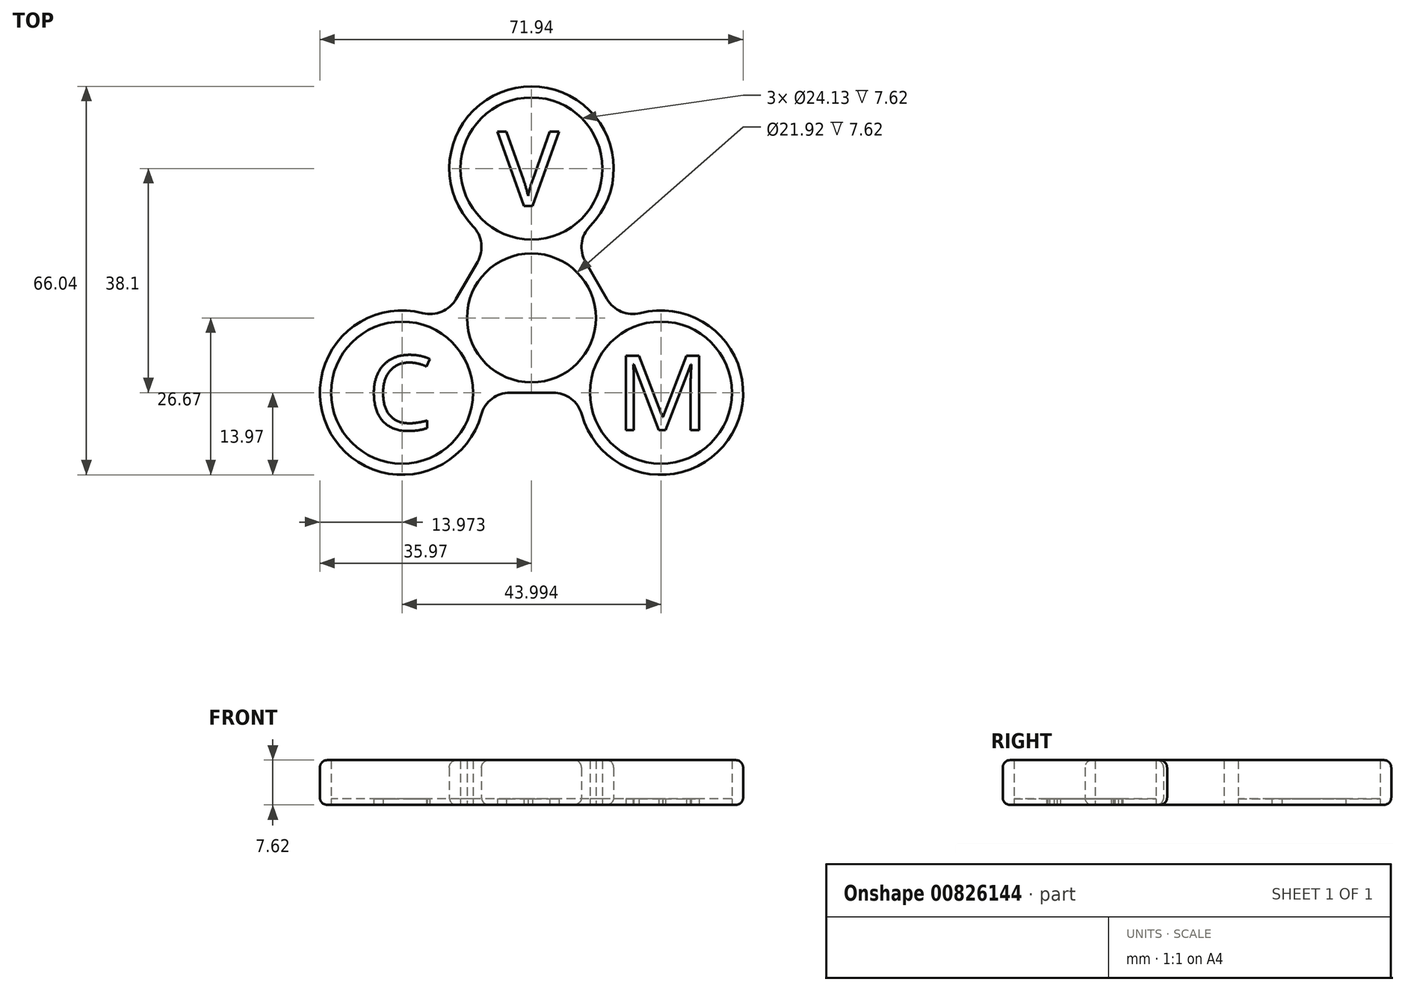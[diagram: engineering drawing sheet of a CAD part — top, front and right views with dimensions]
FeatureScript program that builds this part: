
annotation { "Feature Type Name" : "Feature", "Feature Type Description" : "" }
export const myFeature = defineFeature(function(context is Context, id is Id, definition is map)
    precondition{}
    {
        {
            var Q0;
            Q0=qCreatedBy(makeId("Top.planeOp"),FACE);
            var sketch = newSketch(context, id + "F0", { "sketchPlane" : qUnion([Q0])});
            skCircle(sketch, "E0.cCircle", {"center": v(0, 0) * mm, "radius": 12.7 * mm, "construction": true});
            skLineSegment(sketch, "E0.0", {"start": v(22, -12.7) * mm, "end": v(-22, -12.7) * mm});
            skLineSegment(sketch, "E0.1", {"start": v(-22, -12.7) * mm, "end": v(0, 25.4) * mm});
            skLineSegment(sketch, "E0.2", {"start": v(0, 25.4) * mm, "end": v(22, -12.7) * mm});
            skPoint(sketch, "E0.0.midPoint", {"position": v(0, -12.7) * mm});
            skCircle(sketch, "E1", {"center": v(0, 25.4) * mm, "radius": 13.97 * mm});
            skCircle(sketch, "E2", {"center": v(-22, -12.7) * mm, "radius": 13.97 * mm});
            skCircle(sketch, "E3", {"center": v(22, -12.7) * mm, "radius": 13.97 * mm});
            skCircle(sketch, "E4", {"center": v(0, 0) * mm, "radius": 10.96 * mm});
            skCircle(sketch, "E5", {"center": v(0, 25.4) * mm, "radius": 12.07 * mm});
            skCircle(sketch, "E6", {"center": v(-22, -12.7) * mm, "radius": 12.07 * mm});
            skCircle(sketch, "E7", {"center": v(22, -12.7) * mm, "radius": 12.07 * mm});
            skText(sketch, "E8", { "text": "C", "fontName": "OpenSans-Regular.ttf"});
            skText(sketch, "E9", { "text": "M", "fontName": "OpenSans-Regular.ttf"});
            skText(sketch, "E10", { "text": "V", "fontName": "OpenSans-Regular.ttf"});
            const initialGuessF0  = {"E8": [-0.02787, -0.01905, 1, 0, 0.0127], "E9": [0.01432, -0.01905, 1, 0, 0.0127], "E10": [-0.00582, 0.01905, 1, 0, 0.0127]};
            skSetInitialGuess(sketch, initialGuessF0);
            skSolve(sketch);
        }
        {
            var Q0;
            {var subQ0=sQuery(id+"F0.wireOp",EDGE,"E0.1");var subQ1=sQuery(id+"F0.wireOp",EDGE,"E0.0");var subQ2=makeQuery(id+"F0.imprint","INTERSECT",VERTEX,{"derivedFrom":[subQ1,subQ0]});Q0=makeQuery(id+"F0.imprint","IMPRINT",FACE,{"disambiguationData":[TD([[makeQuery(id+"F0.imprint","IMPRINT",EDGE,{"disambiguationData":[TD([[subQ2,1.0]])],"derivedFrom":subQ1}),1.0]])]});}
            var Q1;
            {var subQ0=sQuery(id+"F0.wireOp",EDGE,"E0.2");var subQ1=sQuery(id+"F0.wireOp",EDGE,"E0.0");var subQ2=makeQuery(id+"F0.imprint","INTERSECT",VERTEX,{"derivedFrom":[subQ1,subQ0]});Q1=makeQuery(id+"F0.imprint","IMPRINT",FACE,{"disambiguationData":[TD([[makeQuery(id+"F0.imprint","IMPRINT",EDGE,{"disambiguationData":[TD([[subQ2,-1.0]])],"derivedFrom":subQ1}),-1.0]])]});}
            var Q2;
            {var subQ0=sQuery(id+"F0.wireOp",EDGE,"E0.2");var subQ1=sQuery(id+"F0.wireOp",EDGE,"E0.0");var subQ2=makeQuery(id+"F0.imprint","INTERSECT",VERTEX,{"derivedFrom":[subQ1,subQ0]});Q2=makeQuery(id+"F0.imprint","IMPRINT",FACE,{"disambiguationData":[TD([[makeQuery(id+"F0.imprint","IMPRINT",EDGE,{"disambiguationData":[TD([[subQ2,-1.0]])],"derivedFrom":subQ1}),1.0]])]});}
            var Q3;
            {var subQ0=sQuery(id+"F0.wireOp",EDGE,"E0.2");var subQ1=sQuery(id+"F0.wireOp",EDGE,"E0.1");var subQ2=makeQuery(id+"F0.imprint","INTERSECT",VERTEX,{"derivedFrom":[subQ1,subQ0]});Q3=makeQuery(id+"F0.imprint","IMPRINT",FACE,{"disambiguationData":[TD([[makeQuery(id+"F0.imprint","IMPRINT",EDGE,{"disambiguationData":[TD([[subQ2,1.0]])],"derivedFrom":subQ1}),-1.0]])]});}
            var Q4;
            {var subQ0=sQuery(id+"F0.wireOp",EDGE,"E0.2");var subQ1=sQuery(id+"F0.wireOp",EDGE,"E0.1");var subQ2=makeQuery(id+"F0.imprint","INTERSECT",VERTEX,{"derivedFrom":[subQ1,subQ0]});Q4=makeQuery(id+"F0.imprint","IMPRINT",FACE,{"disambiguationData":[TD([[makeQuery(id+"F0.imprint","IMPRINT",EDGE,{"disambiguationData":[TD([[subQ2,1.0]])],"derivedFrom":subQ1}),1.0]])]});}
            var Q5;
            {var subQ0=sQuery(id+"F0.wireOp",EDGE,"E0.1");var subQ1=sQuery(id+"F0.wireOp",EDGE,"E0.0");var subQ2=makeQuery(id+"F0.imprint","INTERSECT",VERTEX,{"derivedFrom":[subQ1,subQ0]});Q5=makeQuery(id+"F0.imprint","IMPRINT",FACE,{"disambiguationData":[TD([[makeQuery(id+"F0.imprint","IMPRINT",EDGE,{"disambiguationData":[TD([[subQ2,1.0]])],"derivedFrom":subQ1}),-1.0]])]});}
            var Q6;
            {var subQ0=sQuery(id+"F0.wireOp",EDGE,"E10.sketch_text.stroke-2");Q6=makeQuery(id+"F0.imprint","IMPRINT",FACE,{"disambiguationData":[TD([[makeQuery(id+"F0.imprint","IMPRINT",EDGE,{"derivedFrom":subQ0}),1.0]])]});}
            var Q7;
            {var subQ1=sQuery(id+"F0.wireOp",EDGE,"E9.sketch_text.stroke-1");Q7=makeQuery(id+"F0.imprint","IMPRINT",FACE,{"disambiguationData":[TD([[makeQuery(id+"F0.imprint","IMPRINT",EDGE,{"derivedFrom":subQ1}),1.0]])]});}
            extrude(context, id + "F1", {"entities" : qUnion([Q0, Q1, Q2, Q3, Q4, Q5, Q6, Q7]), "depth" : 1.02 * mm, "offsetDistance" : 25.4 * mm});
        }
        {
            var Q0;
            {var subQ0=sQuery(id+"F0.wireOp",EDGE,"E1");var subQ1=sQuery(id+"F0.wireOp",EDGE,"E0.1");var subQ2=makeQuery(id+"F0.imprint","INTERSECT",VERTEX,{"derivedFrom":[subQ1,subQ0]});Q0=makeQuery(id+"F0.imprint","IMPRINT",FACE,{"disambiguationData":[TD([[makeQuery(id+"F0.imprint","IMPRINT",EDGE,{"disambiguationData":[TD([[subQ2,-1.0]])],"derivedFrom":subQ1}),1.0]])]});}
            var Q1;
            {var subQ0=sQuery(id+"F0.wireOp",EDGE,"E2");var subQ1=sQuery(id+"F0.wireOp",EDGE,"E0.0");var subQ2=makeQuery(id+"F0.imprint","INTERSECT",VERTEX,{"derivedFrom":[subQ1,subQ0]});Q1=makeQuery(id+"F0.imprint","IMPRINT",FACE,{"disambiguationData":[TD([[makeQuery(id+"F0.imprint","IMPRINT",EDGE,{"disambiguationData":[TD([[subQ2,-1.0]])],"derivedFrom":subQ1}),1.0]])]});}
            var Q2;
            {var subQ0=sQuery(id+"F0.wireOp",EDGE,"E3");var subQ1=sQuery(id+"F0.wireOp",EDGE,"E0.0");var subQ2=makeQuery(id+"F0.imprint","INTERSECT",VERTEX,{"derivedFrom":[subQ1,subQ0]});Q2=makeQuery(id+"F0.imprint","IMPRINT",FACE,{"disambiguationData":[TD([[makeQuery(id+"F0.imprint","IMPRINT",EDGE,{"disambiguationData":[TD([[subQ2,1.0]])],"derivedFrom":subQ1}),-1.0]])]});}
            var Q3;
            {var subQ0=sQuery(id+"F0.wireOp",EDGE,"E3");var subQ1=sQuery(id+"F0.wireOp",EDGE,"E0.0");var subQ2=makeQuery(id+"F0.imprint","INTERSECT",VERTEX,{"derivedFrom":[subQ1,subQ0]});Q3=makeQuery(id+"F0.imprint","IMPRINT",FACE,{"disambiguationData":[TD([[makeQuery(id+"F0.imprint","IMPRINT",EDGE,{"disambiguationData":[TD([[subQ2,1.0]])],"derivedFrom":subQ1}),1.0]])]});}
            var Q4;
            {var subQ0=sQuery(id+"F0.wireOp",EDGE,"E2");var subQ1=sQuery(id+"F0.wireOp",EDGE,"E0.0");var subQ2=makeQuery(id+"F0.imprint","INTERSECT",VERTEX,{"derivedFrom":[subQ1,subQ0]});Q4=makeQuery(id+"F0.imprint","IMPRINT",FACE,{"disambiguationData":[TD([[makeQuery(id+"F0.imprint","IMPRINT",EDGE,{"disambiguationData":[TD([[subQ2,-1.0]])],"derivedFrom":subQ1}),-1.0]])]});}
            var Q5;
            Q5=makeQuery(id+"F0.imprint","IMPRINT",FACE,{"disambiguationData":[TD([[makeQuery(id+"F0.imprint","IMPRINT",EDGE,{"derivedFrom":sQuery(id+"F0.wireOp",EDGE,"E4")}),-1.0]])]});
            var Q6;
            {var subQ0=sQuery(id+"F0.wireOp",EDGE,"E1");var subQ1=sQuery(id+"F0.wireOp",EDGE,"E0.1");var subQ2=makeQuery(id+"F0.imprint","INTERSECT",VERTEX,{"derivedFrom":[subQ1,subQ0]});Q6=makeQuery(id+"F0.imprint","IMPRINT",FACE,{"disambiguationData":[TD([[makeQuery(id+"F0.imprint","IMPRINT",EDGE,{"disambiguationData":[TD([[subQ2,-1.0]])],"derivedFrom":subQ1}),-1.0]])]});}
            extrude(context, id + "F2", {"entities" : qUnion([Q0, Q1, Q2, Q3, Q4, Q5, Q6]), "depth" : 7.62 * mm, "offsetDistance" : 25.4 * mm});
        }
        {
            var Q0;
            Q0=makeQuery(id+"F2.opExtrude","SWEPT_EDGE",EDGE,{"disambiguationData":[OSD([sQuery(id+"F0.wireOp",EDGE,"E0.1"),sQuery(id+"F0.wireOp",EDGE,"E2")])]});
            var Q1;
            Q1=makeQuery(id+"F2.opExtrude","SWEPT_EDGE",EDGE,{"disambiguationData":[OSD([sQuery(id+"F0.wireOp",EDGE,"E0.2"),sQuery(id+"F0.wireOp",EDGE,"E3")])]});
            var Q2;
            Q2=makeQuery(id+"F2.opExtrude","SWEPT_EDGE",EDGE,{"disambiguationData":[OSD([sQuery(id+"F0.wireOp",EDGE,"E0.2"),sQuery(id+"F0.wireOp",EDGE,"E1")])]});
            var Q3;
            Q3=makeQuery(id+"F2.opExtrude","SWEPT_EDGE",EDGE,{"disambiguationData":[OSD([sQuery(id+"F0.wireOp",EDGE,"E0.1"),sQuery(id+"F0.wireOp",EDGE,"E1")])]});
            var Q4;
            Q4=makeQuery(id+"F2.opExtrude","SWEPT_EDGE",EDGE,{"disambiguationData":[OSD([sQuery(id+"F0.wireOp",EDGE,"E0.0"),sQuery(id+"F0.wireOp",EDGE,"E3")])]});
            var Q5;
            Q5=makeQuery(id+"F2.opExtrude","SWEPT_EDGE",EDGE,{"disambiguationData":[OSD([sQuery(id+"F0.wireOp",EDGE,"E0.0"),sQuery(id+"F0.wireOp",EDGE,"E2")])]});
            fillet(context, id + "F3", {"entities" : qUnion([Q0, Q1, Q2, Q3, Q4, Q5]), "radius" : 5.08 * mm, "tangentPropagation" : true, "allowEdgeOverflow" : false});
        }
        {
            var Q0;
            Q0=makeQuery(id+"F2.opExtrude","CAP_EDGE",EDGE,{"disambiguationData":[OSD([sQuery(id+"F0.wireOp",EDGE,"E1")])],"isStart":false});
            var Q1;
            {var subQ0=sQuery(id+"F0.wireOp",EDGE,"E1");var subQ1=sQuery(id+"F0.wireOp",EDGE,"E0.1");Q1=makeQuery(id+"F3.opFillet","BLEND_EDGE",EDGE,{"blendedFrom":[makeQuery(id+"F2.opExtrude","SWEPT_EDGE",EDGE,{"disambiguationData":[OSD([subQ1,subQ0])]}),makeQuery(id+"F2.opExtrude","CAP_FACE",FACE,{"disambiguationData":[OSD([sQuery(id+"F0.wireOp",EDGE,"E0.0"),subQ1,sQuery(id+"F0.wireOp",EDGE,"E0.2"),subQ0,sQuery(id+"F0.wireOp",EDGE,"E2"),sQuery(id+"F0.wireOp",EDGE,"E3"),sQuery(id+"F0.wireOp",EDGE,"E4"),sQuery(id+"F0.wireOp",EDGE,"E5"),sQuery(id+"F0.wireOp",EDGE,"E6"),sQuery(id+"F0.wireOp",EDGE,"E7")])],"isStart":true})],"blendedInto":[makeQuery(id+"F2.opExtrude","CAP_FACE",FACE,{"disambiguationData":[OSD([sQuery(id+"F0.wireOp",EDGE,"E0.0"),subQ1,sQuery(id+"F0.wireOp",EDGE,"E0.2"),subQ0,sQuery(id+"F0.wireOp",EDGE,"E2"),sQuery(id+"F0.wireOp",EDGE,"E3"),sQuery(id+"F0.wireOp",EDGE,"E4"),sQuery(id+"F0.wireOp",EDGE,"E5"),sQuery(id+"F0.wireOp",EDGE,"E6"),sQuery(id+"F0.wireOp",EDGE,"E7")])],"isStart":true})]});}
            fillet(context, id + "F4", {"entities" : qUnion([Q0, Q1]), "radius" : 1.27 * mm, "tangentPropagation" : true, "allowEdgeOverflow" : false});
        }
    });
